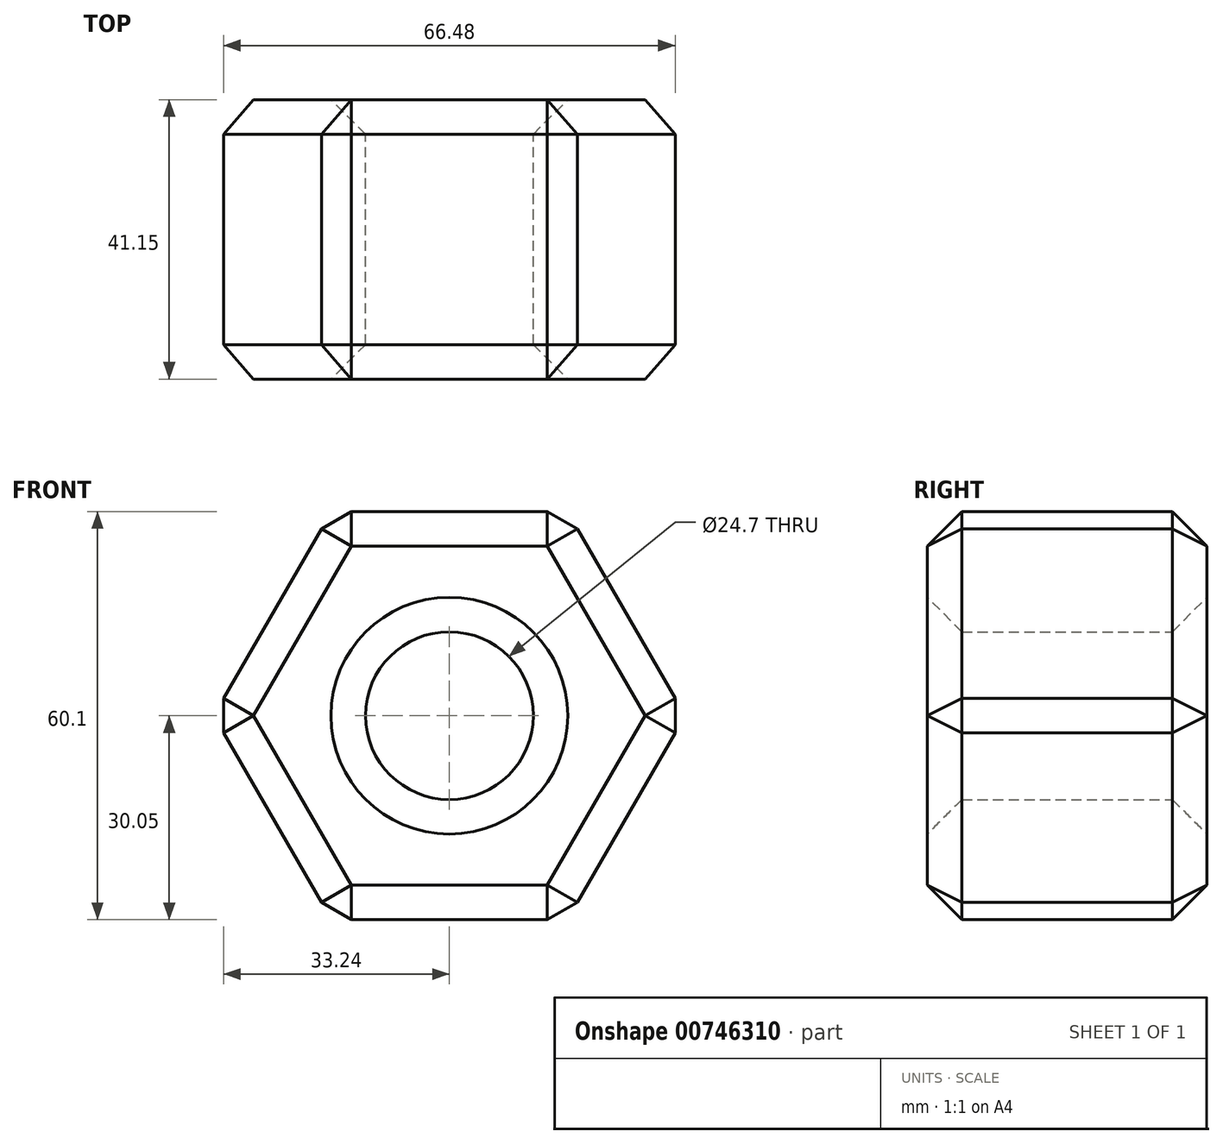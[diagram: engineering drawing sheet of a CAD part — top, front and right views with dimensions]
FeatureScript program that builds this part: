
annotation { "Feature Type Name" : "Feature", "Feature Type Description" : "" }
export const myFeature = defineFeature(function(context is Context, id is Id, definition is map)
    precondition{}
    {
        {
            var Q0;
            Q0=qCreatedBy(makeId("Front.planeOp"),FACE);
            var sketch = newSketch(context, id + "F0", { "sketchPlane" : qUnion([Q0])});
            skCircle(sketch, "E0.cCircle", {"center": v(0, 0) * mm, "radius": 30.05 * mm, "construction": true});
            skLineSegment(sketch, "E0.0", {"start": v(17.35, -30.05) * mm, "end": v(-17.35, -30.05) * mm});
            skLineSegment(sketch, "E0.1", {"start": v(-17.35, -30.05) * mm, "end": v(-34.7, 0) * mm});
            skLineSegment(sketch, "E0.2", {"start": v(-34.7, 0) * mm, "end": v(-17.35, 30.05) * mm});
            skLineSegment(sketch, "E0.3", {"start": v(-17.35, 30.05) * mm, "end": v(17.35, 30.05) * mm});
            skLineSegment(sketch, "E0.4", {"start": v(17.35, 30.05) * mm, "end": v(34.7, 0) * mm});
            skLineSegment(sketch, "E0.5", {"start": v(34.7, 0) * mm, "end": v(17.35, -30.05) * mm});
            skPoint(sketch, "E0.0.midPoint", {"position": v(0, -30.05) * mm});
            skCircle(sketch, "E1", {"center": v(0, 0) * mm, "radius": 12.35 * mm});
            skSolve(sketch);
        }
        {
            var Q0;
            Q0 = qSketchRegion(id + "F0", true);
            extrude(context, id + "F1", {"entities" : qUnion([Q0]), "depth" : 41.15 * mm, "offsetDistance" : 25.4 * mm});
        }
        {
            var Q0;
            Q0=makeQuery(id+"F1.opExtrude","CAP_FACE",FACE,{"disambiguationData":[OSD([sQuery(id+"F0.wireOp",EDGE,"E0.0"),sQuery(id+"F0.wireOp",EDGE,"E0.1"),sQuery(id+"F0.wireOp",EDGE,"E0.2"),sQuery(id+"F0.wireOp",EDGE,"E0.3"),sQuery(id+"F0.wireOp",EDGE,"E0.4"),sQuery(id+"F0.wireOp",EDGE,"E0.5"),sQuery(id+"F0.wireOp",EDGE,"E1")])],"isStart":false});
            var Q1;
            Q1=makeQuery(id+"F1.opExtrude","CAP_FACE",FACE,{"disambiguationData":[OSD([sQuery(id+"F0.wireOp",EDGE,"E0.0"),sQuery(id+"F0.wireOp",EDGE,"E0.1"),sQuery(id+"F0.wireOp",EDGE,"E0.2"),sQuery(id+"F0.wireOp",EDGE,"E0.3"),sQuery(id+"F0.wireOp",EDGE,"E0.4"),sQuery(id+"F0.wireOp",EDGE,"E0.5"),sQuery(id+"F0.wireOp",EDGE,"E1")])],"isStart":true});
            var Q2;
            Q2=makeQuery(id+"F1.opExtrude","SWEPT_FACE",FACE,{"disambiguationData":[OSD([sQuery(id+"F0.wireOp",EDGE,"E0.4")])]});
            var Q3;
            Q3=makeQuery(id+"F1.opExtrude","SWEPT_FACE",FACE,{"disambiguationData":[OSD([sQuery(id+"F0.wireOp",EDGE,"E0.5")])]});
            var Q4;
            Q4=makeQuery(id+"F1.opExtrude","SWEPT_FACE",FACE,{"disambiguationData":[OSD([sQuery(id+"F0.wireOp",EDGE,"E0.3")])]});
            var Q5;
            Q5=makeQuery(id+"F1.opExtrude","SWEPT_FACE",FACE,{"disambiguationData":[OSD([sQuery(id+"F0.wireOp",EDGE,"E0.2")])]});
            var Q6;
            Q6=makeQuery(id+"F1.opExtrude","SWEPT_FACE",FACE,{"disambiguationData":[OSD([sQuery(id+"F0.wireOp",EDGE,"E0.0")])]});
            chamfer(context, id + "F2", {"entities" : qUnion([Q0, Q1, Q2, Q3, Q4, Q5, Q6]), "width" : 5.08 * mm, "tangentPropagation" : true});
        }
    });
